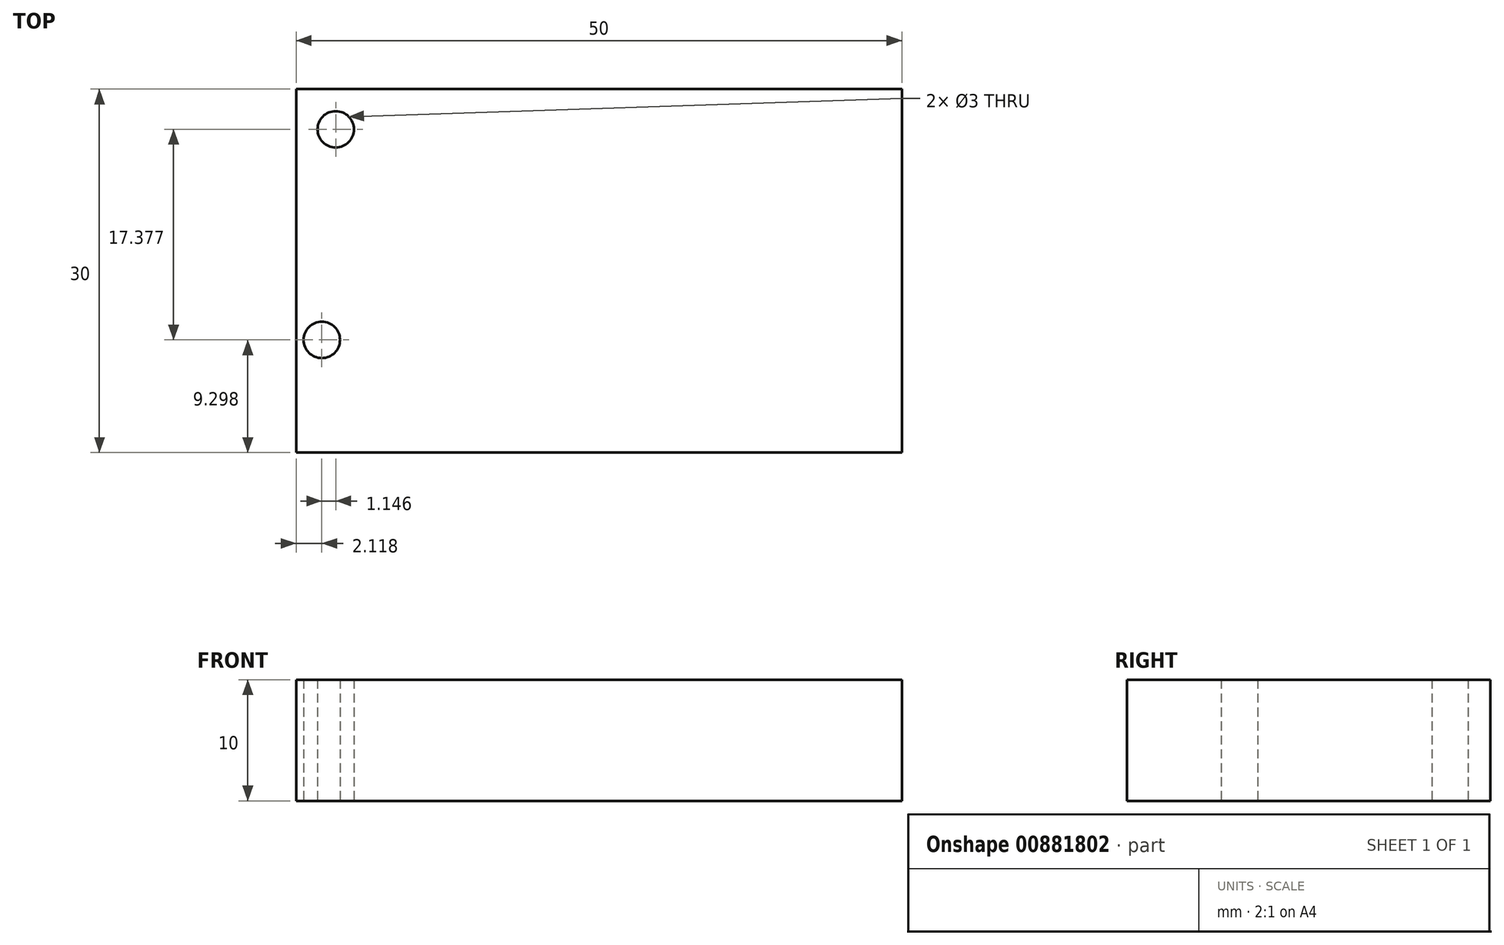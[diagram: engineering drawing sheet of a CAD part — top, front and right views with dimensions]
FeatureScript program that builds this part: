
annotation { "Feature Type Name" : "Feature", "Feature Type Description" : "" }
export const myFeature = defineFeature(function(context is Context, id is Id, definition is map)
    precondition{}
    {
        {
            var Q0;
            Q0=qCreatedBy(makeId("Top.planeOp"),FACE);
            var sketch = newSketch(context, id + "F0", { "sketchPlane" : qUnion([Q0])});
            skLineSegment(sketch, "E0.bottom", {"start": v(-23.6, 7.24) * mm, "end": v(26.4, 7.24) * mm});
            skLineSegment(sketch, "E0.top", {"start": v(-23.6, -22.76) * mm, "end": v(26.4, -22.76) * mm});
            skLineSegment(sketch, "E0.left", {"start": v(-23.6, 7.24) * mm, "end": v(-23.6, -22.76) * mm});
            skLineSegment(sketch, "E0.right", {"start": v(26.4, 7.24) * mm, "end": v(26.4, -22.76) * mm});
            skCircle(sketch, "E1", {"center": v(-20.34, 3.91) * mm, "radius": 1.5 * mm});
            skCircle(sketch, "E2", {"center": v(-21.48, -13.46) * mm, "radius": 1.5 * mm});
            skSolve(sketch);
        }
        {
            var Q0;
            Q0=makeQuery(id+"F0.imprint","IMPRINT",FACE,{"disambiguationData":[TD([[makeQuery(id+"F0.imprint","IMPRINT",EDGE,{"derivedFrom":sQuery(id+"F0.wireOp",EDGE,"E0.bottom")}),-1.0]])]});
            extrude(context, id + "F1", {"entities" : qUnion([Q0]), "depth" : 10 * mm, "offsetDistance" : 25.4 * mm});
        }
    });
